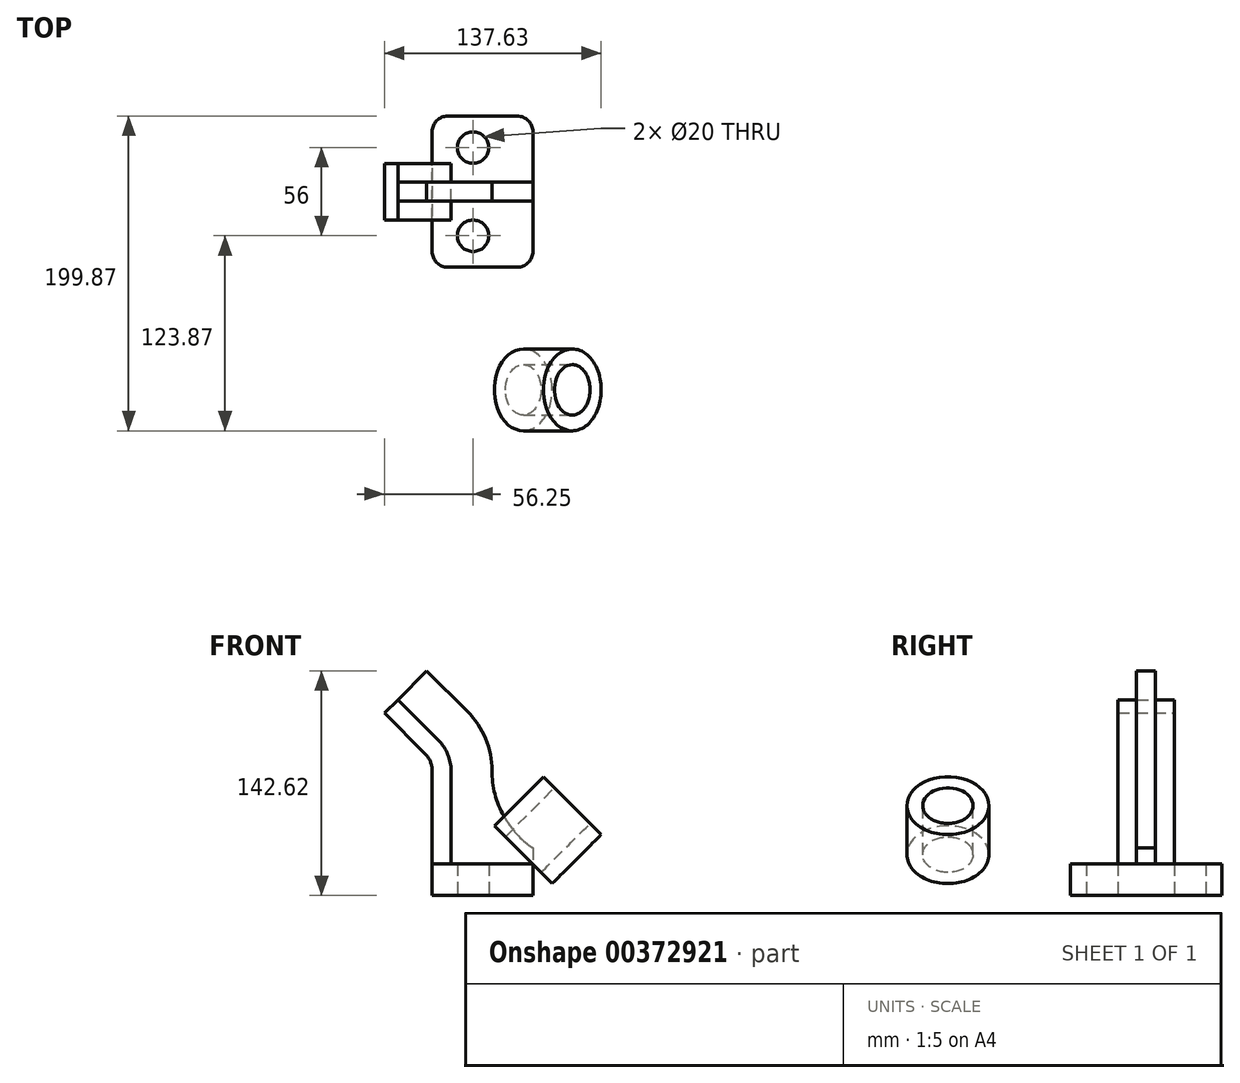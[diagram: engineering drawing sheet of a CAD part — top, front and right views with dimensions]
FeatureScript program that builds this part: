
annotation { "Feature Type Name" : "Feature", "Feature Type Description" : "" }
export const myFeature = defineFeature(function(context is Context, id is Id, definition is map)
    precondition{}
    {
        {
            var Q0;
            Q0=qCreatedBy(makeId("Top.planeOp"),FACE);
            var sketch = newSketch(context, id + "F0", { "sketchPlane" : qUnion([Q0])});
            skLineSegment(sketch, "E0.bottom", {"start": v(22, 48) * mm, "end": v(-22, 48) * mm});
            skLineSegment(sketch, "E0.top", {"start": v(22, -48) * mm, "end": v(-22, -48) * mm});
            skLineSegment(sketch, "E0.left", {"start": v(32, 38) * mm, "end": v(32, -38) * mm});
            skLineSegment(sketch, "E0.right", {"start": v(-32, 38) * mm, "end": v(-32, -38) * mm});
            skLineSegment(sketch, "E1", {"start": v(67.59, 0) * mm, "end": v(-65.42, 0) * mm, "construction": true});
            skPoint(sketch, "E2.visualSharp", {"position": v(32, 48) * mm});
            skArc(sketch, "E2.filletArc", {"start": v(32, 38) * mm, "mid": v(29.07, 45.07) * mm, "end": v(22, 48) * mm});
            skPoint(sketch, "E3.visualSharp", {"position": v(-32, 48) * mm});
            skArc(sketch, "E3.filletArc", {"start": v(-22, 48) * mm, "mid": v(-29.07, 45.07) * mm, "end": v(-32, 38) * mm});
            skPoint(sketch, "E4.visualSharp", {"position": v(-32, -48) * mm});
            skArc(sketch, "E4.filletArc", {"start": v(-32, -38) * mm, "mid": v(-29.07, -45.07) * mm, "end": v(-22, -48) * mm});
            skPoint(sketch, "E5.visualSharp", {"position": v(32, -48) * mm});
            skArc(sketch, "E5.filletArc", {"start": v(22, -48) * mm, "mid": v(29.07, -45.07) * mm, "end": v(32, -38) * mm});
            skLineSegment(sketch, "E6", {"start": v(0, 70.28) * mm, "end": v(0, -83.89) * mm, "construction": true});
            skCircle(sketch, "E7", {"center": v(-6, -28) * mm, "radius": 10 * mm});
            skCircle(sketch, "E8.MirrorC", {"center": v(-6, 28) * mm, "radius": 10 * mm});
            skSolve(sketch);
        }
        {
            var Q0;
            Q0=makeQuery(id+"F0.imprint","IMPRINT",FACE,{"disambiguationData":[TD([[makeQuery(id+"F0.imprint","IMPRINT",EDGE,{"derivedFrom":sQuery(id+"F0.wireOp",EDGE,"E0.bottom")}),1.0]])]});
            extrude(context, id + "F1", {"entities" : qUnion([Q0]), "depth" : 20 * mm});
        }
        {
            var Q0;
            Q0=qCreatedBy(makeId("Front.planeOp"),FACE);
            var sketch = newSketch(context, id + "F2", { "sketchPlane" : qUnion([Q0])});
            skLineSegment(sketch, "E9", {"start": v(-32, 20) * mm, "end": v(-32, 79.28) * mm});
            skLineSegment(sketch, "E10", {"start": v(-32, 0) * mm, "end": v(-32, 146) * mm, "construction": true});
            skPoint(sketch, "E10.endSnap0", {"position": v(-32, 49.64) * mm});
            skLineSegment(sketch, "E11", {"start": v(6, 146) * mm, "end": v(-32, 146) * mm, "construction": true});
            skLineSegment(sketch, "E12", {"start": v(-32, 146) * mm, "end": v(-114.02, 228.02) * mm});
            skLineSegment(sketch, "E13", {"start": v(6, 79.28) * mm, "end": v(-32, 79.28) * mm});
            skLineSegment(sketch, "E14", {"start": v(-20, 79.28) * mm, "end": v(-20, 20) * mm});
            skLineSegment(sketch, "E15", {"start": v(6, 79.28) * mm, "end": v(85.97, 79.28) * mm, "construction": true});
            skArc(sketch, "E16", {"start": v(6, 79.28) * mm, "mid": v(12.9, 51.48) * mm, "end": v(32, 30.14) * mm});
            skPoint(sketch, "E17.end.orphan", {"position": v(70.68, 20) * mm});
            skLineSegment(sketch, "E18", {"start": v(32, 30.14) * mm, "end": v(32, 20) * mm});
            skArc(sketch, "E19", {"start": v(-32, 79.28) * mm, "mid": v(-33.14, 85.03) * mm, "end": v(-36.4, 89.9) * mm});
            skPoint(sketch, "E20.start.orphan", {"position": v(-47, 97.17) * mm});
            skArc(sketch, "E21.0", {"start": v(-20, 79.28) * mm, "mid": v(-22.06, 89.62) * mm, "end": v(-27.9, 98.38) * mm});
            skArc(sketch, "E22.0", {"start": v(6, 79.28) * mm, "mid": v(1.97, 99.57) * mm, "end": v(-9.52, 116.76) * mm});
            skLineSegment(sketch, "E23", {"start": v(-36.4, 89.9) * mm, "end": v(-120.1, 173.6) * mm});
            skLineSegment(sketch, "E24.0", {"start": v(-27.9, 98.38) * mm, "end": v(-111.61, 182.08) * mm});
            skLineSegment(sketch, "E25.0", {"start": v(-9.52, 116.76) * mm, "end": v(-93.23, 200.47) * mm});
            skLineSegment(sketch, "E26", {"start": v(32, 20) * mm, "end": v(-32, 20) * mm});
            skLineSegment(sketch, "E27", {"start": v(-32, 146) * mm, "end": v(-62.25, 115.75) * mm});
            skSolve(sketch);
        }
        {
            var Q0;
            Q0=sQuery(id+"F2.wireOp",EDGE,"E12");
            extrude(context, id + "F3", {"bodyType" : ToolBodyType.SURFACE, "surfaceEntities" : qUnion([Q0]), "depth" : 50 * mm, "hasSecondDirection" : true, "secondDirectionOppositeDirection" : true, "secondDirectionDepth" : 50 * mm});
        }
        {
            var Q0;
            Q0=makeQuery(id+"F3.opExtrude","SWEPT_FACE",FACE,{"disambiguationData":[OSD([sQuery(id+"F2.wireOp",EDGE,"E12")])]});
            var sketch = newSketch(context, id + "F4", { "sketchPlane" : qUnion([Q0])});
            skCircle(sketch, "E28", {"center": v(-125.87, 0) * mm, "radius": 32 * mm});
            skCircle(sketch, "E29", {"center": v(-125.87, 0) * mm, "radius": 26 * mm});
            skCircle(sketch, "E30", {"center": v(-125.87, 0) * mm, "radius": 16 * mm});
            skSolve(sketch);
        }
        {
            var Q0;
            {var subQ0=sQuery(id+"F4.wireOp",EDGE,"E29");var subQ1=makeQuery(id+"F3.opExtrude","SWEPT_EDGE",EDGE,{"disambiguationData":[OSD([sQuery(id+"F2.wireOp",VERTEX,"E12.start")])]});var subQ2=makeQuery(id+"F4.imprint","INTERSECT",VERTEX,{"disambiguationData":[OD(0.0)],"derivedFrom":[subQ1,subQ0]});Q0=makeQuery(id+"F4.imprint","IMPRINT",FACE,{"disambiguationData":[TD([[makeQuery(id+"F4.imprint","IMPRINT",EDGE,{"disambiguationData":[TD([[subQ2,1.0]])],"derivedFrom":subQ0}),1.0]])]});}
            var Q1;
            {var subQ0=sQuery(id+"F4.wireOp",EDGE,"E29");var subQ1=makeQuery(id+"F3.opExtrude","SWEPT_EDGE",EDGE,{"disambiguationData":[OSD([sQuery(id+"F2.wireOp",VERTEX,"E12.start")])]});var subQ2=makeQuery(id+"F4.imprint","INTERSECT",VERTEX,{"disambiguationData":[OD(0.0)],"derivedFrom":[subQ1,subQ0]});Q1=makeQuery(id+"F4.imprint","IMPRINT",FACE,{"disambiguationData":[TD([[makeQuery(id+"F4.imprint","IMPRINT",EDGE,{"disambiguationData":[TD([[subQ2,-1.0]])],"derivedFrom":subQ0}),1.0]])]});}
            extrude(context, id + "F5", {"entities" : qUnion([Q0, Q1]), "oppositeDirection" : true, "depth" : 32 * mm});
        }
        {
            var Q0;
            Q0=makeQuery(id+"F5.opExtrude","CAP_FACE",FACE,{"disambiguationData":[OSD([sQuery(id+"F4.wireOp",EDGE,"E29"),sQuery(id+"F4.wireOp",EDGE,"E30")])],"isStart":false});
            var sketch = newSketch(context, id + "F6", { "sketchPlane" : qUnion([Q0])});
            skCircle(sketch, "E31", {"center": v(-125.87, 0) * mm, "radius": 32 * mm});
            skSolve(sketch);
        }
        {
            var Q0;
            Q0=makeQuery(id+"F6.imprint","IMPRINT",FACE,{"disambiguationData":[TD([[makeQuery(id+"F6.imprint","IMPRINT",EDGE,{"derivedFrom":sQuery(id+"F6.wireOp",EDGE,"E31")}),1.0]])]});
            var Q1;
            Q1=makeQuery(id+"F6.imprint","IMPRINT",FACE,{"disambiguationData":[TD([[makeQuery(id+"F6.imprint","IMPRINT",EDGE,{"derivedFrom":makeQuery(id+"F5.opExtrude","CAP_EDGE",EDGE,{"disambiguationData":[OSD([sQuery(id+"F4.wireOp",EDGE,"E29")])],"isStart":false})}),-1.0]])]});
            var Q2;
            Q2=makeQuery(id+"F6.imprint","IMPRINT",FACE,{"disambiguationData":[TD([[makeQuery(id+"F6.imprint","IMPRINT",EDGE,{"derivedFrom":makeQuery(id+"F5.opExtrude","CAP_EDGE",EDGE,{"disambiguationData":[OSD([sQuery(id+"F4.wireOp",EDGE,"E30")])],"isStart":false})}),-1.0]])]});
            var Q3;
            Q3=sQuery(id+"F6.wireOp",EDGE,"E31");
            extrude(context, id + "F7", {"entities" : qUnion([Q0, Q1, Q2]), "operationType" : NewBodyOperationType.ADD, "surfaceEntities" : qUnion([Q3]), "depth" : 12 * mm});
        }
        {
            var Q0;
            {var subQ0=sQuery(id+"F2.wireOp",EDGE,"E9");Q0=makeQuery(id+"F2.imprint","IMPRINT",FACE,{"disambiguationData":[TD([[makeQuery(id+"F2.imprint","IMPRINT",EDGE,{"derivedFrom":subQ0}),-1.0]])]});}
            var Q1;
            {var subQ1=sQuery(id+"F2.wireOp",EDGE,"E19");Q1=makeQuery(id+"F2.imprint","IMPRINT",FACE,{"disambiguationData":[TD([[makeQuery(id+"F2.imprint","IMPRINT",EDGE,{"derivedFrom":subQ1}),-1.0]])]});}
            extrude(context, id + "F8", {"entities" : qUnion([Q0, Q1]), "depth" : 18 * mm, "hasSecondDirection" : true, "secondDirectionOppositeDirection" : true, "secondDirectionDepth" : 18 * mm});
        }
        {
            var Q0;
            {var subQ2=sQuery(id+"F2.wireOp",EDGE,"E14");Q0=makeQuery(id+"F2.imprint","IMPRINT",FACE,{"disambiguationData":[TD([[makeQuery(id+"F2.imprint","IMPRINT",EDGE,{"derivedFrom":subQ2}),1.0]])]});}
            var Q1;
            {var subQ1=sQuery(id+"F2.wireOp",EDGE,"E21.0");Q1=makeQuery(id+"F2.imprint","IMPRINT",FACE,{"disambiguationData":[TD([[makeQuery(id+"F2.imprint","IMPRINT",EDGE,{"derivedFrom":subQ1}),-1.0]])]});}
            extrude(context, id + "F9", {"entities" : qUnion([Q0, Q1]), "depth" : 6 * mm, "hasSecondDirection" : true, "secondDirectionOppositeDirection" : true, "secondDirectionDepth" : 6 * mm});
        }
        {
            var Q0;
            Q0=makeQuery(id+"F5.opExtrude","CAP_FACE",FACE,{"disambiguationData":[OSD([sQuery(id+"F4.wireOp",EDGE,"E29"),sQuery(id+"F4.wireOp",EDGE,"E30")])],"isStart":true});
            var sketch = newSketch(context, id + "F10", { "sketchPlane" : qUnion([Q0])});
            skCircle(sketch, "E32", {"center": v(-125.87, 0) * mm, "radius": 16 * mm});
            skSolve(sketch);
        }
        {
            var Q0;
            Q0=makeQuery(id+"F7.boolean.opBoolean","SPLIT",FACE,{"disambiguationData":[TD([makeQuery(id+"F5.opExtrude","SWEPT_FACE",FACE,{"disambiguationData":[OSD([sQuery(id+"F4.wireOp",EDGE,"E30")])]})])],"derivedFrom":makeQuery(id+"F7.opExtrude","CAP_FACE",FACE,{"disambiguationData":[OSD([sQuery(id+"F6.wireOp",EDGE,"E31")])],"isStart":true})});
            extrude(context, id + "F11", {"entities" : qUnion([Q0]), "operationType" : NewBodyOperationType.REMOVE, "oppositeDirection" : true, "depth" : 32 * mm});
        }
        {
            var Q0;
            Q0=makeQuery(id+"F10.imprint","IMPRINT",FACE,{"disambiguationData":[TD([[makeQuery(id+"F10.imprint","IMPRINT",EDGE,{"derivedFrom":sQuery(id+"F10.wireOp",EDGE,"E32")}),1.0]])]});
            extrude(context, id + "F12", {"entities" : qUnion([Q0]), "operationType" : NewBodyOperationType.REMOVE, "oppositeDirection" : true, "depth" : 60 * mm});
        }
    });
